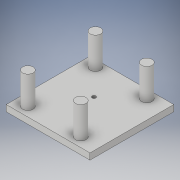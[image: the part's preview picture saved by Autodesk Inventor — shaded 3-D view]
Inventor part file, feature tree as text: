
AUTODESK INVENTOR PART (.ipt)
format: ipt  version: 2019 (Build 230136000, 136)  size: 118,784 bytes
history: native  units: mm
features: sketch x4, extrude x2, hole x1
ambient origin geometry x8: Origin, YZ Plane, XZ Plane, XY Plane, X Axis, Y Axis, Z Axis, Center Point
bodies: Solid1 (feature_tree)
feature tree (7):
  extrude  "Extrusion1"  Depth=400.0mm
  extrude  "Extrusion2"  Depth=30.0mm TaperAngle=0.0deg
  sketch  "Sketch3"  dims[d5=50.0mm d6=50.0mm]
  hole  "Hole1"  [1 undecoded]
  sketch  "Sketch1"  dims[d0=400.0mm d1=400.0mm]
  sketch  "Sketch2"  dims[d2=400.0mm d3=30.0mm d4=0.0mm]
  sketch  "Sketch4"  dims[d7=50.0mm d8=50.0mm d9=150.0mm d10=0.0mm d11=17.894mm d12=30.0mm d13=4.0mm d14=2.0mm d15=90.0deg d16=53.975mm d17=20.594885mm]
note: 1 required parameter value undecoded (feature->parameter linkage not recoverable at this tier; creation-order binding heuristic only, values carry confidence <= 0.55)
